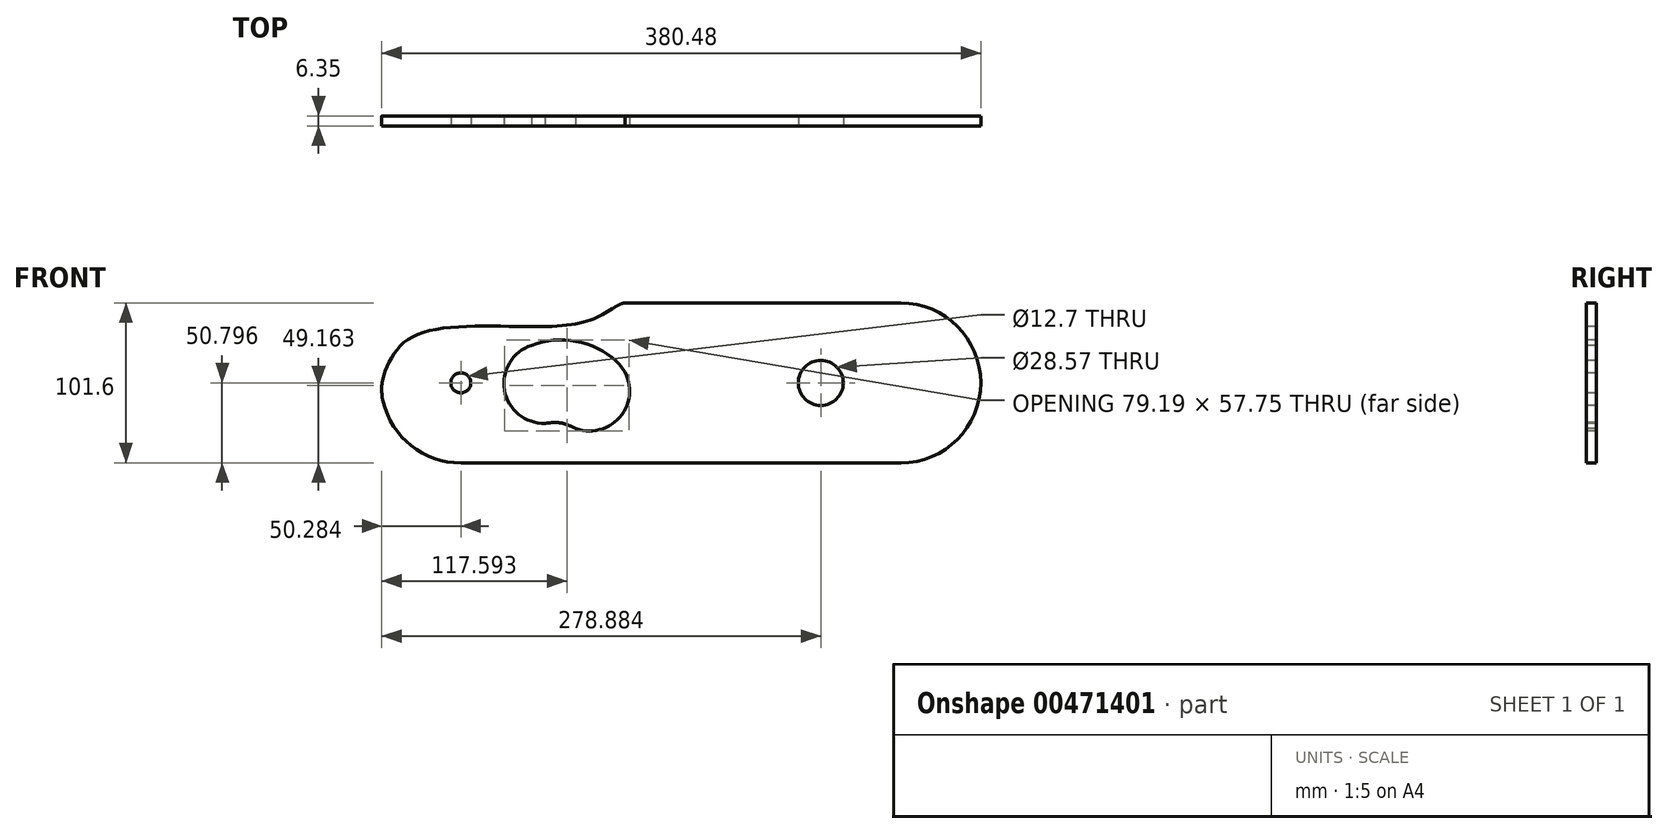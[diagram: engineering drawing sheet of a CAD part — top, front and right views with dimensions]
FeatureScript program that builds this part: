
annotation { "Feature Type Name" : "Feature", "Feature Type Description" : "" }
export const myFeature = defineFeature(function(context is Context, id is Id, definition is map)
    precondition{}
    {
        {
            var Q0;
            Q0=qCreatedBy(makeId("Front.planeOp"),FACE);
            var sketch = newSketch(context, id + "F0", { "sketchPlane" : qUnion([Q0])});
            skLineSegment(sketch, "E0.bottom", {"start": v(-121.55, 165.79) * mm, "end": v(53.5, 165.79) * mm});
            skLineSegment(sketch, "E0.top", {"start": v(-225.9, 267.39) * mm, "end": v(53.5, 267.39) * mm});
            skLineSegment(sketch, "E1", {"start": v(-276.7, 216.59) * mm, "end": v(104.3, 216.59) * mm, "construction": true});
            skLineSegment(sketch, "E2", {"start": v(-86.2, 267.39) * mm, "end": v(-86.2, 165.79) * mm, "construction": true});
            skCircle(sketch, "E3", {"center": v(53.5, 216.59) * mm, "radius": 50.8 * mm});
            skArc(sketch, "E4", {"start": v(-189.9, 180.73) * mm, "mid": v(-206.5, 263.54) * mm, "end": v(-276.7, 216.59) * mm});
            skFitSpline(sketch, "E5", {"points": [v(-276.7, 216.59) * mm, v(-253.4, 185.77) * mm, v(-156.78, 179.7) * mm, v(-124.4, 165.79) * mm], "startDerivative": vector(47.43, -131.99) * mm, "endDerivative": vector(91.44, -65.54) * mm});
            skLineSegment(sketch, "E6", {"start": v(-225.9, 267.39) * mm, "end": v(-225.9, 216.59) * mm, "construction": true});
            skLineSegment(sketch, "E7", {"start": v(53.5, 267.39) * mm, "end": v(53.5, 216.59) * mm, "construction": true});
            skLineSegment(sketch, "E8", {"start": v(53.5, 165.79) * mm, "end": v(53.5, 216.59) * mm, "construction": true});
            skPoint(sketch, "E9", {"position": v(-189.9, 180.73) * mm});
            skCircle(sketch, "E10", {"center": v(-225.9, 216.59) * mm, "radius": 6.35 * mm});
            skPoint(sketch, "E11", {"position": v(-162.4, 241.99) * mm});
            skArc(sketch, "E12", {"start": v(-210.74, 267.39) * mm, "mid": v(-211.25, 266.39) * mm, "end": v(-211.74, 265.38) * mm});
            skLineSegment(sketch, "E13", {"start": v(-162.4, 241.99) * mm, "end": v(-125.85, 201.4) * mm, "construction": true});
            skLineSegment(sketch, "E14", {"start": v(-162.4, 241.99) * mm, "end": v(-183.92, 191.8) * mm, "construction": true});
            skPoint(sketch, "E15", {"position": v(-144.12, 221.7) * mm});
            skPoint(sketch, "E16", {"position": v(-173.16, 216.9) * mm});
            skCircle(sketch, "E17", {"center": v(-173.16, 216.9) * mm, "radius": 25.4 * mm});
            skCircle(sketch, "E18", {"center": v(-144.12, 221.7) * mm, "radius": 25.4 * mm});
            skArc(sketch, "E19", {"start": v(-163.15, 240.24) * mm, "mid": v(-162.08, 240.1) * mm, "end": v(-161.12, 240.57) * mm});
            skArc(sketch, "E20", {"start": v(-183.17, 193.55) * mm, "mid": v(-153.79, 189.99) * mm, "end": v(-127.12, 202.82) * mm});
            skFitSpline(sketch, "E21", {"points": [v(-129.47, 169.34) * mm, v(-119.73, 165.79) * mm, v(-91.95, 181.85) * mm], "startDerivative": vector(23.89, -16.09) * mm, "endDerivative": vector(48.9, 36.33) * mm});
            skCircle(sketch, "E22", {"center": v(2.7, 216.59) * mm, "radius": 14.29 * mm});
            skFitSpline(sketch, "E23", {"points": [v(-172.41, 242.28) * mm, v(-162.4, 241.99) * mm, v(-153, 245.5) * mm], "startDerivative": vector(20.35, -2.5) * mm, "endDerivative": vector(18.46, 8.91) * mm});
            skSolve(sketch);
        }
        {
            var Q0;
            Q0=makeQuery(id+"F0.imprint","IMPRINT",FACE,{"disambiguationData":[TD([[makeQuery(id+"F0.imprint","IMPRINT",EDGE,{"derivedFrom":sQuery(id+"F0.wireOp",EDGE,"E10")}),-1.0]])]});
            var Q1;
            {var subQ12=sQuery(id+"F0.wireOp",EDGE,"E12");Q1=makeQuery(id+"F0.imprint","IMPRINT",FACE,{"disambiguationData":[TD([[makeQuery(id+"F0.imprint","IMPRINT",EDGE,{"derivedFrom":subQ12}),1.0]])]});}
            var Q2;
            {var subQ0=sQuery(id+"F0.wireOp",EDGE,"E20");var subQ1=sQuery(id+"F0.wireOp",EDGE,"E4");var subQ2=makeQuery(id+"F0.imprint","INTERSECT",VERTEX,{"derivedFrom":[subQ1,subQ0]});Q2=makeQuery(id+"F0.imprint","IMPRINT",FACE,{"disambiguationData":[TD([[makeQuery(id+"F0.imprint","IMPRINT",EDGE,{"disambiguationData":[TD([[subQ2,-1.0]])],"derivedFrom":subQ1}),1.0]])]});}
            var Q3;
            {var subQ3=sQuery(id+"F0.wireOp",EDGE,"E12");Q3=makeQuery(id+"F0.imprint","IMPRINT",FACE,{"disambiguationData":[TD([[makeQuery(id+"F0.imprint","IMPRINT",EDGE,{"derivedFrom":subQ3}),-1.0]])]});}
            var Q4;
            {var subQ0=sQuery(id+"F0.wireOp",EDGE,"E23");var subQ1=sQuery(id+"F0.wireOp",EDGE,"E18");var subQ2=makeQuery(id+"F0.imprint","INTERSECT",VERTEX,{"disambiguationData":[OD(0.0)],"derivedFrom":[subQ1,subQ0]});Q4=makeQuery(id+"F0.imprint","IMPRINT",FACE,{"disambiguationData":[TD([[makeQuery(id+"F0.imprint","IMPRINT",EDGE,{"disambiguationData":[TD([[subQ2,-1.0]])],"derivedFrom":subQ1}),1.0]])]});}
            var Q5;
            {var subQ0=sQuery(id+"F0.wireOp",EDGE,"E23");var subQ1=sQuery(id+"F0.wireOp",EDGE,"E17");var subQ2=makeQuery(id+"F0.imprint","INTERSECT",VERTEX,{"disambiguationData":[OD(0.0)],"derivedFrom":[subQ1,subQ0]});Q5=makeQuery(id+"F0.imprint","IMPRINT",FACE,{"disambiguationData":[TD([[makeQuery(id+"F0.imprint","IMPRINT",EDGE,{"disambiguationData":[TD([[subQ2,1.0]])],"derivedFrom":subQ1}),1.0]])]});}
            var Q6;
            {var subQ0=sQuery(id+"F0.wireOp",EDGE,"E21");var subQ1=sQuery(id+"F0.wireOp",EDGE,"E0.bottom");var subQ2=makeQuery(id+"F0.imprint","INTERSECT",VERTEX,{"disambiguationData":[OD(0.0)],"derivedFrom":[subQ1,subQ0]});Q6=makeQuery(id+"F0.imprint","IMPRINT",FACE,{"disambiguationData":[TD([[makeQuery(id+"F0.imprint","IMPRINT",EDGE,{"disambiguationData":[TD([[subQ2,-1.0]])],"derivedFrom":subQ1}),-1.0]])]});}
            var Q7;
            {var subQ0=sQuery(id+"F0.wireOp",EDGE,"E3");var subQ1=makeQuery(id+"F0.imprint","INTERSECT",VERTEX,{"derivedFrom":[sQuery(id+"F0.wireOp",EDGE,"E0.top"),subQ0]});Q7=makeQuery(id+"F0.imprint","IMPRINT",FACE,{"disambiguationData":[TD([[makeQuery(id+"F0.imprint","IMPRINT",EDGE,{"disambiguationData":[TD([[subQ1,-1.0]])],"derivedFrom":subQ0}),1.0]])]});}
            extrude(context, id + "F1", {"entities" : qUnion([Q0, Q1, Q2, Q3, Q4, Q5, Q6, Q7]), "depth" : 6.35 * mm});
        }
        {
            var Q0;
            Q0=makeQuery(id+"F1.opExtrude","SWEPT_EDGE",EDGE,{"disambiguationData":[OSD([sQuery(id+"F0.wireOp",EDGE,"E4"),sQuery(id+"F0.wireOp",EDGE,"E5")])]});
            fillet(context, id + "F2", {"entities" : qUnion([Q0]), "radius" : 32.03 * mm, "tangentPropagation" : true, "allowEdgeOverflow" : false});
        }
        {
            var Q0;
            Q0=makeQuery(id+"F1.opExtrude","SWEPT_BODY",BODY,{"disambiguationData":[OSD([sQuery(id+"F0.wireOp",EDGE,"E0.bottom"),sQuery(id+"F0.wireOp",EDGE,"E0.top"),sQuery(id+"F0.wireOp",EDGE,"E3"),sQuery(id+"F0.wireOp",EDGE,"E4"),sQuery(id+"F0.wireOp",EDGE,"E5"),sQuery(id+"F0.wireOp",EDGE,"E10"),sQuery(id+"F0.wireOp",EDGE,"E17"),sQuery(id+"F0.wireOp",EDGE,"E18"),sQuery(id+"F0.wireOp",EDGE,"E20"),sQuery(id+"F0.wireOp",EDGE,"E21"),sQuery(id+"F0.wireOp",EDGE,"E22"),sQuery(id+"F0.wireOp",EDGE,"E23")])]});
            var Q1;
            Q1=makeQuery(id+"F1.opExtrude","CAP_EDGE",EDGE,{"disambiguationData":[OSD([sQuery(id+"F0.wireOp",EDGE,"E0.top")])],"isStart":false});
            transform(context, id + "F3", {"entities" : qUnion([Q0]), "transformType" : TransformType.ROTATION, "transformAxis" : qUnion([Q1]), "angle" : 180 * degree, "makeCopy" : false});
        }
    });
